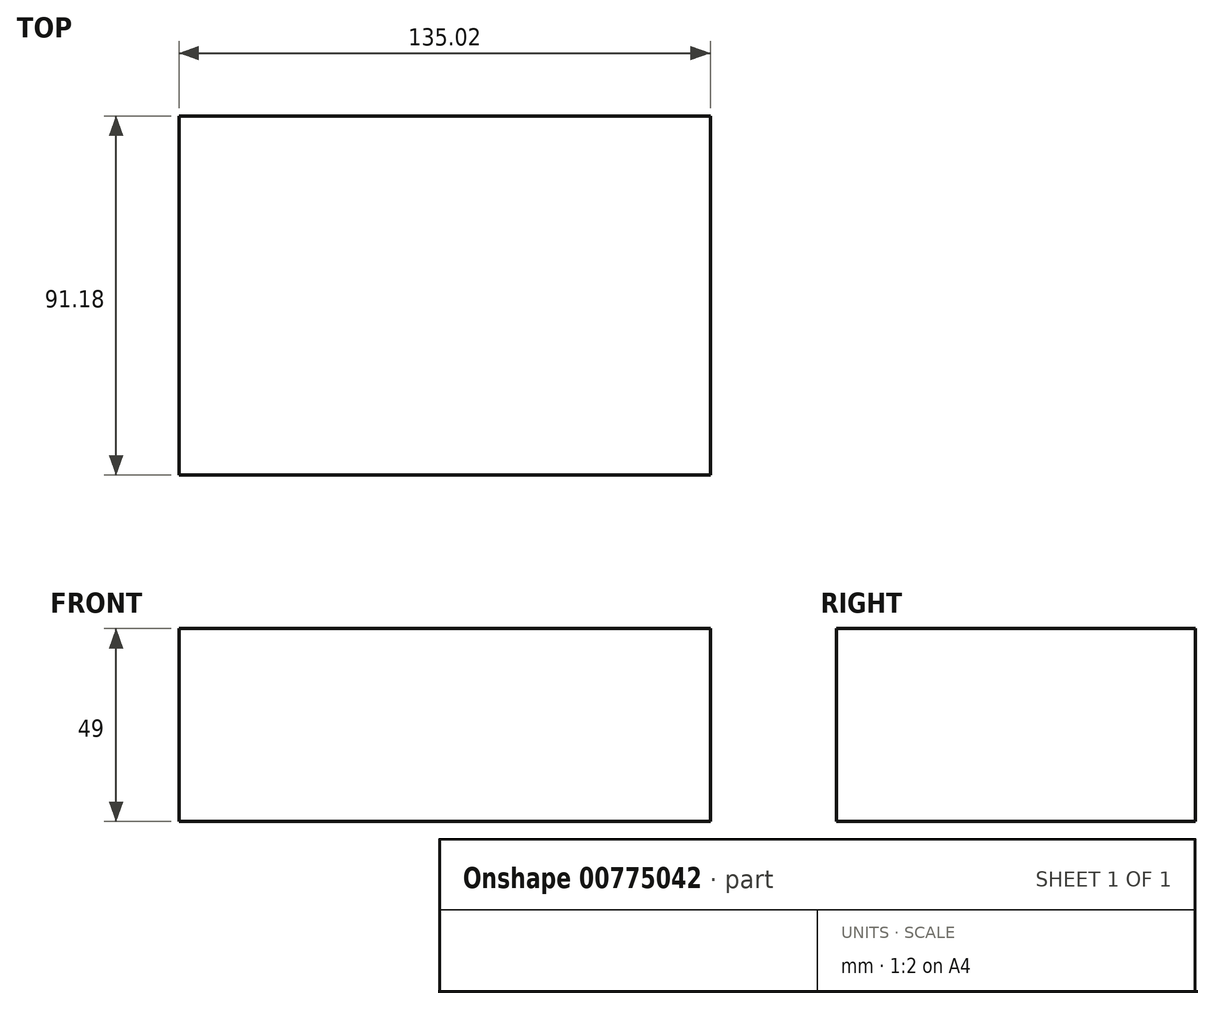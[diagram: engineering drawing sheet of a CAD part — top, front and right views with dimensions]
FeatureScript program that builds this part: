
annotation { "Feature Type Name" : "Feature", "Feature Type Description" : "" }
export const myFeature = defineFeature(function(context is Context, id is Id, definition is map)
    precondition{}
    {
        {
            var Q0;
            Q0=qCreatedBy(makeId("Top.planeOp"),FACE);
            var sketch = newSketch(context, id + "F0", { "sketchPlane" : qUnion([Q0])});
            skLineSegment(sketch, "E0.bottom", {"start": v(-89.1, 54) * mm, "end": v(45.91, 54) * mm});
            skLineSegment(sketch, "E0.top", {"start": v(-89.1, -37.2) * mm, "end": v(45.91, -37.2) * mm});
            skLineSegment(sketch, "E0.left", {"start": v(-89.1, 54) * mm, "end": v(-89.1, -37.2) * mm});
            skLineSegment(sketch, "E0.right", {"start": v(45.91, 54) * mm, "end": v(45.91, -37.2) * mm});
            skSolve(sketch);
        }
        {
            var Q0;
            Q0 = qSketchRegion(id + "F0", true);
            extrude(context, id + "F1", {"entities" : qUnion([Q0]), "depth" : 49 * mm, "offsetDistance" : 25 * mm});
        }
    });
